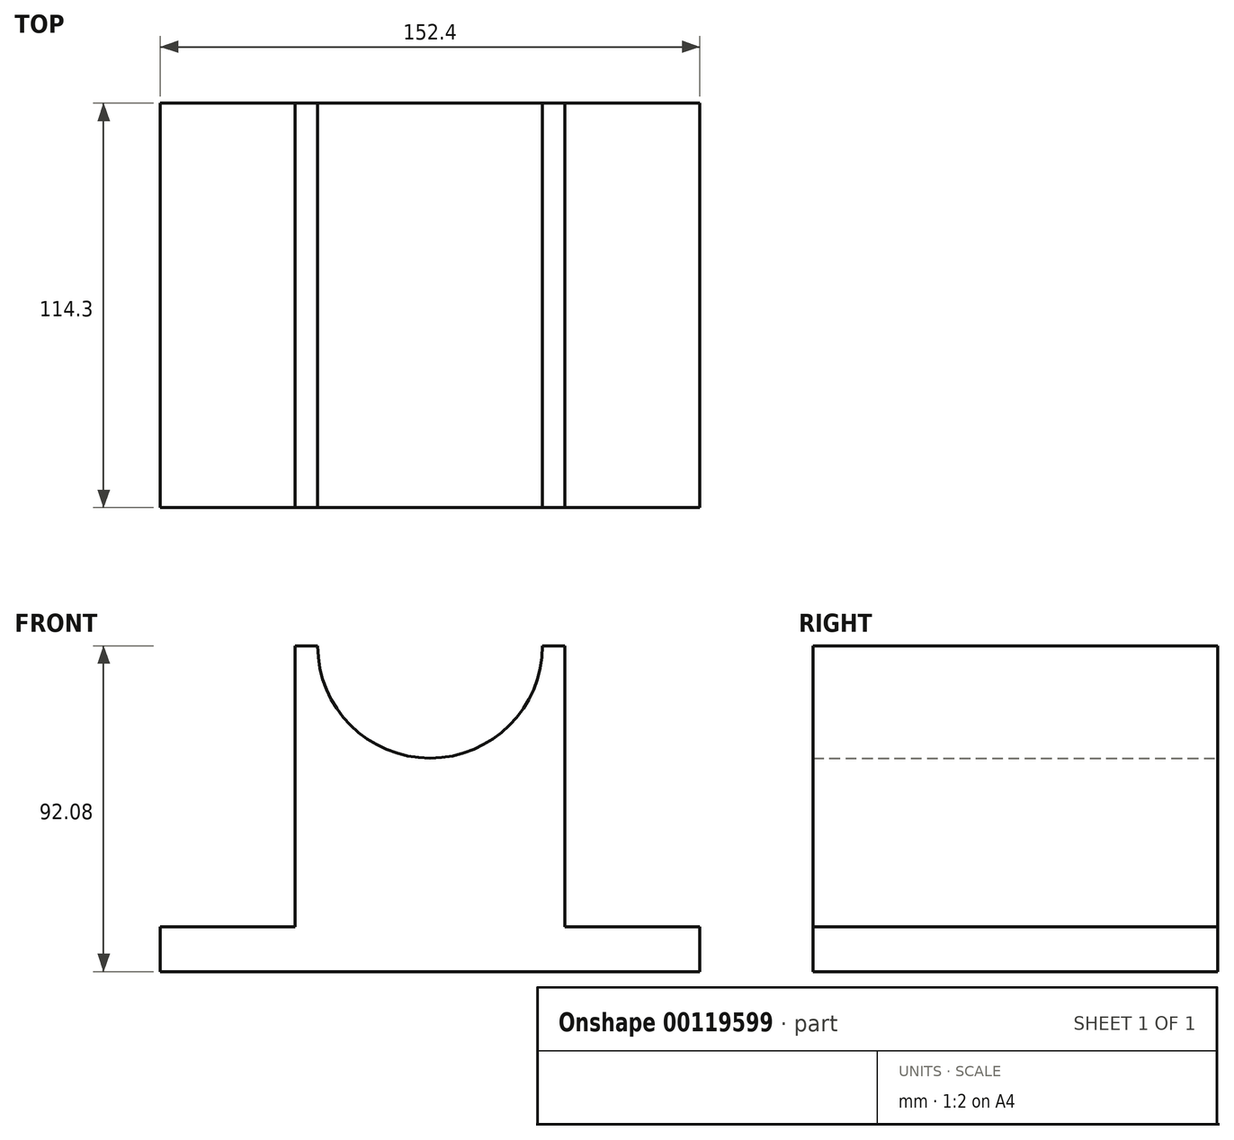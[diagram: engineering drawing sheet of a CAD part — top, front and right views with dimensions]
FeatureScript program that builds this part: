
annotation { "Feature Type Name" : "Feature", "Feature Type Description" : "" }
export const myFeature = defineFeature(function(context is Context, id is Id, definition is map)
    precondition{}
    {
        {
            var Q0;
            Q0=qCreatedBy(makeId("Front.planeOp"),FACE);
            var sketch = newSketch(context, id + "F0", { "sketchPlane" : qUnion([Q0])});
            skLineSegment(sketch, "E0", {"start": v(0, 0) * mm, "end": v(152.4, 0) * mm});
            skLineSegment(sketch, "E1", {"start": v(152.4, 0) * mm, "end": v(152.4, 12.7) * mm});
            skLineSegment(sketch, "E2", {"start": v(152.4, 12.7) * mm, "end": v(114.3, 12.7) * mm});
            skLineSegment(sketch, "E3", {"start": v(114.3, 12.7) * mm, "end": v(114.3, 92.08) * mm});
            skLineSegment(sketch, "E4", {"start": v(114.3, 92.08) * mm, "end": v(107.95, 92.08) * mm});
            skLineSegment(sketch, "E5", {"start": v(44.45, 92.08) * mm, "end": v(38.1, 92.07) * mm});
            skLineSegment(sketch, "E6", {"start": v(38.1, 92.07) * mm, "end": v(38.1, 12.7) * mm});
            skLineSegment(sketch, "E7", {"start": v(38.1, 12.7) * mm, "end": v(0, 12.7) * mm});
            skLineSegment(sketch, "E8", {"start": v(0, 12.7) * mm, "end": v(0, 0) * mm});
            skArc(sketch, "E9", {"start": v(44.45, 92.08) * mm, "mid": v(76.2, 60.33) * mm, "end": v(107.95, 92.08) * mm});
            skSolve(sketch);
        }
        {
            var Q0;
            Q0=makeQuery(id+"F0.imprint","IMPRINT",FACE,{"disambiguationData":[TD([[makeQuery(id+"F0.imprint","IMPRINT",EDGE,{"derivedFrom":sQuery(id+"F0.wireOp",EDGE,"E0")}),1.0]])]});
            var Q1;
            Q1=makeQuery(id+"F0.imprint","IMPRINT",FACE,{"disambiguationData":[TD([[makeQuery(id+"F0.imprint","IMPRINT",EDGE,{"derivedFrom":sQuery(id+"F0.wireOp",EDGE,"hGWaKnEA-IuFU-fmIC-1Y1w-1voNmJuhs11y")}),1.0]])]});
            extrude(context, id + "F1", {"entities" : qUnion([Q0, Q1]), "depth" : 114.3 * mm});
        }
    });
